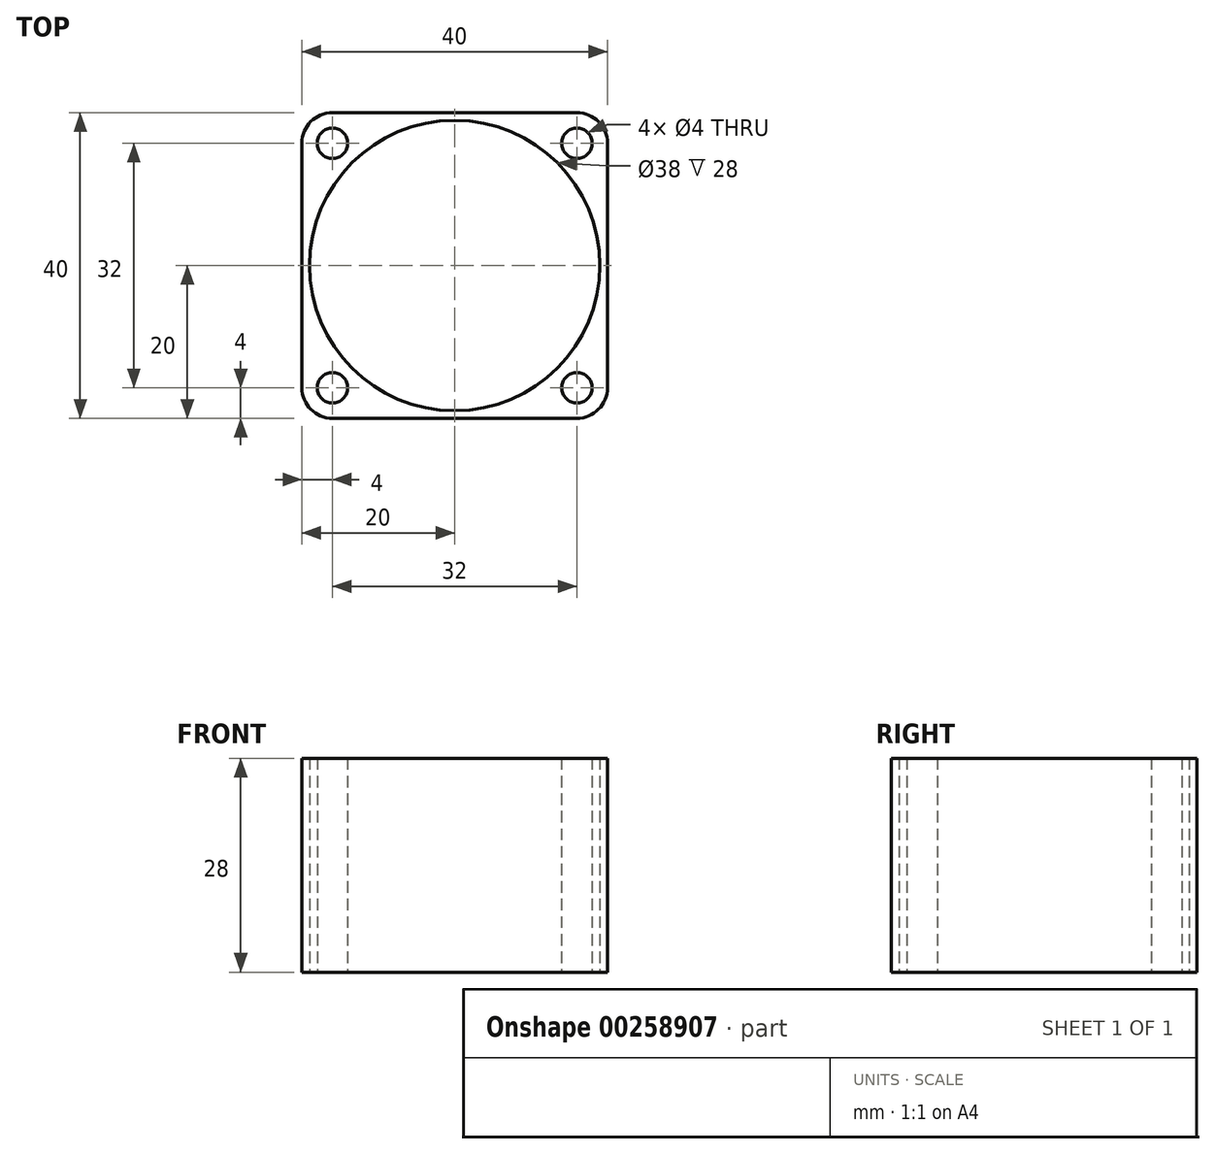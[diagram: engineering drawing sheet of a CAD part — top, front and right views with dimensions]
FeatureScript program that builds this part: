
annotation { "Feature Type Name" : "Feature", "Feature Type Description" : "" }
export const myFeature = defineFeature(function(context is Context, id is Id, definition is map)
    precondition{}
    {
        {
            var Q0;
            Q0=qCreatedBy(makeId("Top.planeOp"),FACE);
            var sketch = newSketch(context, id + "F0", { "sketchPlane" : qUnion([Q0])});
            skLineSegment(sketch, "E0.bottom", {"start": v(-16, -20) * mm, "end": v(16, -20) * mm});
            skLineSegment(sketch, "E0.top", {"start": v(-16, 20) * mm, "end": v(16, 20) * mm});
            skLineSegment(sketch, "E0.left", {"start": v(-20, -16) * mm, "end": v(-20, 16) * mm});
            skLineSegment(sketch, "E0.right", {"start": v(20, -16) * mm, "end": v(20, 16) * mm});
            skPoint(sketch, "E0.middle", {"position": v(0, 0) * mm});
            skPoint(sketch, "E1.visualSharp", {"position": v(-20, 20) * mm});
            skArc(sketch, "E1.filletArc", {"start": v(-16, 20) * mm, "mid": v(-18.83, 18.83) * mm, "end": v(-20, 16) * mm});
            skPoint(sketch, "E2.visualSharp", {"position": v(20, 20) * mm});
            skArc(sketch, "E2.filletArc", {"start": v(20, 16) * mm, "mid": v(18.83, 18.83) * mm, "end": v(16, 20) * mm});
            skPoint(sketch, "E3.visualSharp", {"position": v(20, -20) * mm});
            skArc(sketch, "E3.filletArc", {"start": v(16, -20) * mm, "mid": v(18.83, -18.83) * mm, "end": v(20, -16) * mm});
            skPoint(sketch, "E4.visualSharp", {"position": v(-20, -20) * mm});
            skArc(sketch, "E4.filletArc", {"start": v(-20, -16) * mm, "mid": v(-18.83, -18.83) * mm, "end": v(-16, -20) * mm});
            skCircle(sketch, "E5", {"center": v(16, 16) * mm, "radius": 2 * mm});
            skCircle(sketch, "E6.MirrorC", {"center": v(16, -16) * mm, "radius": 2 * mm});
            skCircle(sketch, "E7.MirrorC", {"center": v(-16, 16) * mm, "radius": 2 * mm});
            skCircle(sketch, "E8.MirrorC", {"center": v(-16, -16) * mm, "radius": 2 * mm});
            skCircle(sketch, "E9", {"center": v(0, 0) * mm, "radius": 19 * mm});
            skSolve(sketch);
        }
        {
            var Q0;
            Q0 = qSketchRegion(id + "F0", true);
            extrude(context, id + "F1", {"entities" : qUnion([Q0]), "depth" : 28 * mm});
        }
    });
